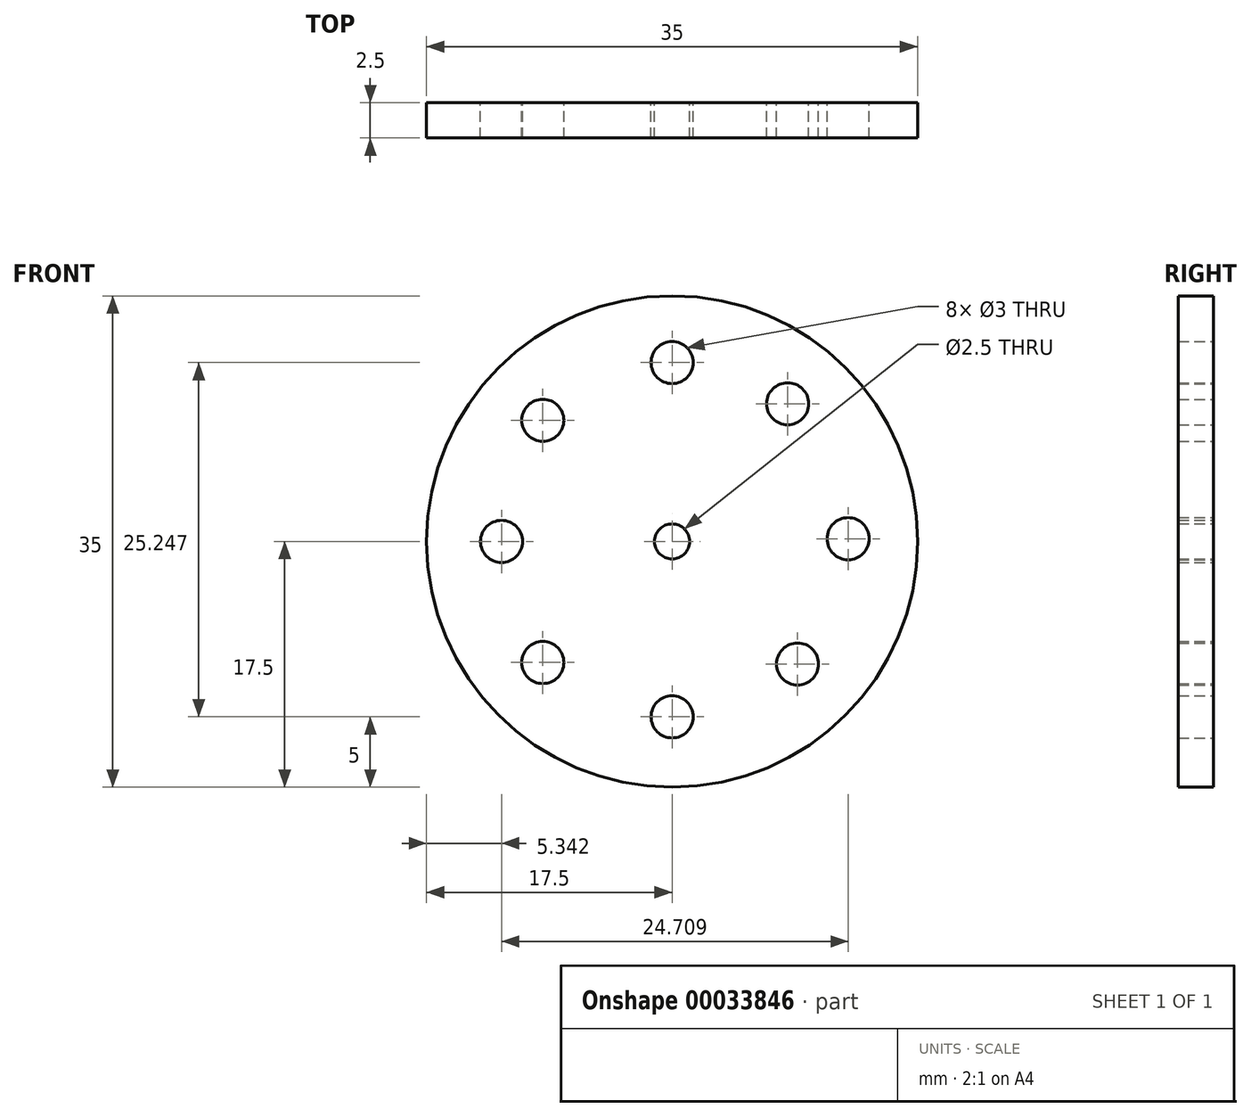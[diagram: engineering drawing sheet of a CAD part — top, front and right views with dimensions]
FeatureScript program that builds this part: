
annotation { "Feature Type Name" : "Feature", "Feature Type Description" : "" }
export const myFeature = defineFeature(function(context is Context, id is Id, definition is map)
    precondition{}
    {
        {
            var Q0;
            Q0=qCreatedBy(makeId("Front.planeOp"),FACE);
            var sketch = newSketch(context, id + "F0", { "sketchPlane" : qUnion([Q0])});
            skCircle(sketch, "E0", {"center": v(0, 0) * mm, "radius": 17.5 * mm});
            skCircle(sketch, "E1", {"center": v(0, 0) * mm, "radius": 2.5 * mm});
            skCircle(sketch, "E2", {"center": v(0, 0) * mm, "radius": 1.25 * mm});
            skCircle(sketch, "E3", {"center": v(0, -12.5) * mm, "radius": 1.5 * mm});
            skCircle(sketch, "E4", {"center": v(8.94, -8.74) * mm, "radius": 1.5 * mm});
            skCircle(sketch, "E5", {"center": v(0, 0) * mm, "radius": 12.5 * mm});
            skCircle(sketch, "E6", {"center": v(12.55, 0.2) * mm, "radius": 1.5 * mm});
            skCircle(sketch, "E7", {"center": v(8.24, 9.8) * mm, "radius": 1.5 * mm});
            skCircle(sketch, "E8", {"center": v(0, 12.75) * mm, "radius": 1.5 * mm});
            skCircle(sketch, "E9", {"center": v(-9.22, 8.63) * mm, "radius": 1.5 * mm});
            skCircle(sketch, "E10", {"center": v(-12.16, 0) * mm, "radius": 1.5 * mm});
            skCircle(sketch, "E11", {"center": v(-9.22, -8.63) * mm, "radius": 1.5 * mm});
            skSolve(sketch);
        }
        {
            var Q0;
            Q0 = qSketchRegion(id + "F0", true);
            var Q1;
            Q1=makeQuery(id+"F0.imprint","IMPRINT",FACE,{"disambiguationData":[TD([[makeQuery(id+"F0.imprint","IMPRINT",EDGE,{"derivedFrom":sQuery(id+"F0.wireOp",EDGE,"E1")}),-1.0]])]});
            var Q2;
            Q2=makeQuery(id+"F0.imprint","IMPRINT",FACE,{"disambiguationData":[TD([[makeQuery(id+"F0.imprint","IMPRINT",EDGE,{"derivedFrom":sQuery(id+"F0.wireOp",EDGE,"E1")}),1.0]])]});
            extrude(context, id + "F1", {"entities" : qUnion([Q0, Q1, Q2]), "depth" : 2.5 * mm});
        }
        {
            var Q0;
            Q0=sQuery(id+"F0.wireOp",EDGE,"E1");
            extrude(context, id + "F2", {"bodyType" : ToolBodyType.SURFACE, "surfaceEntities" : qUnion([Q0]), "depth" : 3.35 * mm});
        }
        {
            var Q0;
            Q0=sQuery(id+"F0.wireOp",EDGE,"E0");
            extrude(context, id + "F3", {"bodyType" : ToolBodyType.SURFACE, "surfaceEntities" : qUnion([Q0]), "depth" : 3.44 * mm});
        }
    });
